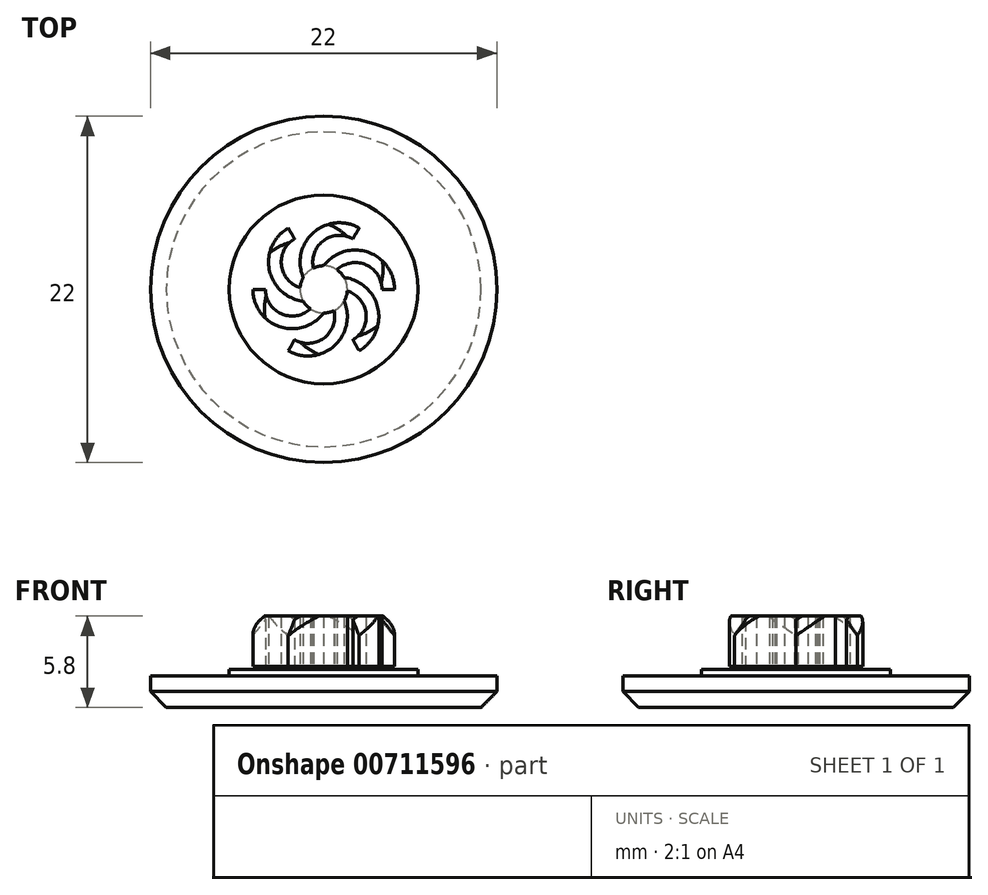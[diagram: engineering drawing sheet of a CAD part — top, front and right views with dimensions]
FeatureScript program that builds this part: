
annotation { "Feature Type Name" : "Feature", "Feature Type Description" : "" }
export const myFeature = defineFeature(function(context is Context, id is Id, definition is map)
    precondition{}
    {
        {
            var Q0;
            Q0=qCreatedBy(makeId("Top.planeOp"),FACE);
            var sketch = newSketch(context, id + "F0", { "sketchPlane" : qUnion([Q0])});
            skCircle(sketch, "E0", {"center": v(0, 0) * mm, "radius": 11 * mm});
            skSolve(sketch);
        }
        {
            var Q0;
            Q0=makeQuery(id+"F0.imprint","IMPRINT",FACE,{"disambiguationData":[TD([[makeQuery(id+"F0.imprint","IMPRINT",EDGE,{"derivedFrom":sQuery(id+"F0.wireOp",EDGE,"E0")}),1.0]])]});
            extrude(context, id + "F1", {"entities" : qUnion([Q0]), "depth" : 2 * mm, "offsetDistance" : 25 * mm});
        }
        {
            var Q0;
            Q0=makeQuery(id+"F1.opExtrude","CAP_EDGE",EDGE,{"disambiguationData":[OSD([sQuery(id+"F0.wireOp",EDGE,"E0")])],"isStart":true});
            chamfer(context, id + "F2", {"entities" : qUnion([Q0]), "width" : 1 * mm, "tangentPropagation" : true});
        }
        {
            var Q0;
            Q0=makeQuery(id+"F1.opExtrude","CAP_FACE",FACE,{"disambiguationData":[OSD([sQuery(id+"F0.wireOp",EDGE,"E0")])],"isStart":false});
            var sketch = newSketch(context, id + "F3", { "sketchPlane" : qUnion([Q0])});
            skCircle(sketch, "E1", {"center": v(0, 0) * mm, "radius": 6 * mm});
            skSolve(sketch);
        }
        {
            var Q0;
            Q0=makeQuery(id+"F3.imprint","IMPRINT",FACE,{"disambiguationData":[TD([[makeQuery(id+"F3.imprint","IMPRINT",EDGE,{"derivedFrom":sQuery(id+"F3.wireOp",EDGE,"E1")}),1.0]])]});
            extrude(context, id + "F4", {"entities" : qUnion([Q0]), "operationType" : NewBodyOperationType.ADD, "depth" : .4 * mm, "offsetDistance" : 25 * mm});
        }
        {
            var Q0;
            Q0=makeQuery(id+"F4.opExtrude","CAP_FACE",FACE,{"disambiguationData":[OSD([sQuery(id+"F3.wireOp",EDGE,"E1")])],"isStart":false});
            var sketch = newSketch(context, id + "F5", { "sketchPlane" : qUnion([Q0])});
            skCircle(sketch, "E2", {"center": v(0, 0) * mm, "radius": 4.5 * mm});
            skCircle(sketch, "E3", {"center": v(0, 0) * mm, "radius": 1.5 * mm});
            skCircle(sketch, "E4.0", {"center": v(0, 0) * mm, "radius": 11 * mm});
            skArc(sketch, "E5", {"start": v(4.5, 0) * mm, "mid": v(2.8, 2.37) * mm, "end": v(0, 1.5) * mm});
            skArc(sketch, "E6.0", {"start": v(3.7, 0) * mm, "mid": v(2.68, 1.56) * mm, "end": v(0.84, 1.24) * mm});
            skLineSegment(sketch, "E7", {"start": v(3.7, 0) * mm, "end": v(4.5, 0) * mm});
            skArc(sketch, "E8.1.0", {"start": v(1.85, 3.2) * mm, "mid": v(-0.01, 3.1) * mm, "end": v(-0.66, 1.35) * mm});
            skArc(sketch, "E8.1.1", {"start": v(2.25, 3.9) * mm, "mid": v(-0.66, 3.6) * mm, "end": v(-1.3, 0.75) * mm});
            skLineSegment(sketch, "E8.1.2", {"start": v(1.85, 3.2) * mm, "end": v(2.25, 3.9) * mm});
            skArc(sketch, "E8.2.0", {"start": v(-1.85, 3.2) * mm, "mid": v(-2.69, 1.54) * mm, "end": v(-1.5, 0.1) * mm});
            skArc(sketch, "E8.2.1", {"start": v(-2.25, 3.9) * mm, "mid": v(-3.45, 1.23) * mm, "end": v(-1.3, -0.75) * mm});
            skLineSegment(sketch, "E8.2.2", {"start": v(-1.85, 3.2) * mm, "end": v(-2.25, 3.9) * mm});
            skArc(sketch, "E8.3.0", {"start": v(-3.7, 0) * mm, "mid": v(-2.68, -1.56) * mm, "end": v(-0.84, -1.24) * mm});
            skArc(sketch, "E8.3.1", {"start": v(-4.5, 0) * mm, "mid": v(-2.8, -2.37) * mm, "end": v(0, -1.5) * mm});
            skLineSegment(sketch, "E8.3.2", {"start": v(-3.7, 0) * mm, "end": v(-4.5, 0) * mm});
            skArc(sketch, "E8.4.0", {"start": v(-1.85, -3.2) * mm, "mid": v(0.01, -3.1) * mm, "end": v(0.66, -1.35) * mm});
            skArc(sketch, "E8.4.1", {"start": v(-2.25, -3.9) * mm, "mid": v(0.66, -3.6) * mm, "end": v(1.3, -0.75) * mm});
            skLineSegment(sketch, "E8.4.2", {"start": v(-1.85, -3.2) * mm, "end": v(-2.25, -3.9) * mm});
            skArc(sketch, "E8.5.0", {"start": v(1.85, -3.2) * mm, "mid": v(2.69, -1.54) * mm, "end": v(1.5, -0.1) * mm});
            skArc(sketch, "E8.5.1", {"start": v(2.25, -3.9) * mm, "mid": v(3.45, -1.23) * mm, "end": v(1.3, 0.75) * mm});
            skLineSegment(sketch, "E8.5.2", {"start": v(1.85, -3.2) * mm, "end": v(2.25, -3.9) * mm});
            skSolve(sketch);
        }
        {
            var Q0;
            {var subQ0=sQuery(id+"F5.wireOp",EDGE,"E8.4.0");Q0=makeQuery(id+"F5.imprint","IMPRINT",FACE,{"disambiguationData":[TD([[makeQuery(id+"F5.imprint","IMPRINT",EDGE,{"derivedFrom":subQ0}),-1.0]])]});}
            var Q1;
            {var subQ0=sQuery(id+"F5.wireOp",EDGE,"E8.3.0");Q1=makeQuery(id+"F5.imprint","IMPRINT",FACE,{"disambiguationData":[TD([[makeQuery(id+"F5.imprint","IMPRINT",EDGE,{"derivedFrom":subQ0}),-1.0]])]});}
            var Q2;
            {var subQ0=sQuery(id+"F5.wireOp",EDGE,"E8.2.0");Q2=makeQuery(id+"F5.imprint","IMPRINT",FACE,{"disambiguationData":[TD([[makeQuery(id+"F5.imprint","IMPRINT",EDGE,{"derivedFrom":subQ0}),-1.0]])]});}
            var Q3;
            {var subQ0=sQuery(id+"F5.wireOp",EDGE,"E8.1.0");Q3=makeQuery(id+"F5.imprint","IMPRINT",FACE,{"disambiguationData":[TD([[makeQuery(id+"F5.imprint","IMPRINT",EDGE,{"derivedFrom":subQ0}),-1.0]])]});}
            var Q4;
            {var subQ0=sQuery(id+"F5.wireOp",EDGE,"E5");Q4=makeQuery(id+"F5.imprint","IMPRINT",FACE,{"disambiguationData":[TD([[makeQuery(id+"F5.imprint","IMPRINT",EDGE,{"derivedFrom":subQ0}),1.0]])]});}
            var Q5;
            {var subQ0=sQuery(id+"F5.wireOp",EDGE,"E8.5.0");Q5=makeQuery(id+"F5.imprint","IMPRINT",FACE,{"disambiguationData":[TD([[makeQuery(id+"F5.imprint","IMPRINT",EDGE,{"derivedFrom":subQ0}),-1.0]])]});}
            var Q6;
            {var subQ0=sQuery(id+"F5.wireOp",EDGE,"E3");var subQ8=makeQuery(id+"F5.imprint","INTERSECT",VERTEX,{"derivedFrom":[subQ0,sQuery(id+"F5.wireOp",EDGE,"E6.0")]});Q6=makeQuery(id+"F5.imprint","IMPRINT",FACE,{"disambiguationData":[TD([[makeQuery(id+"F5.imprint","IMPRINT",EDGE,{"disambiguationData":[TD([[subQ8,1.0]])],"derivedFrom":subQ0}),1.0]])]});}
            extrude(context, id + "F6", {"entities" : qUnion([Q0, Q1, Q2, Q3, Q4, Q5, Q6]), "operationType" : NewBodyOperationType.ADD, "depth" : 3.4 * mm, "offsetDistance" : 25 * mm});
        }
        {
            var Q0;
            {var subQ0=sQuery(id+"F5.wireOp",EDGE,"E8.4.0");Q0=makeQuery(id+"F5.imprint","IMPRINT",FACE,{"disambiguationData":[TD([[makeQuery(id+"F5.imprint","IMPRINT",EDGE,{"derivedFrom":subQ0}),-1.0]])]});}
            var Q1;
            {var subQ0=sQuery(id+"F5.wireOp",EDGE,"E8.3.0");Q1=makeQuery(id+"F5.imprint","IMPRINT",FACE,{"disambiguationData":[TD([[makeQuery(id+"F5.imprint","IMPRINT",EDGE,{"derivedFrom":subQ0}),-1.0]])]});}
            var Q2;
            {var subQ0=sQuery(id+"F5.wireOp",EDGE,"E8.2.0");Q2=makeQuery(id+"F5.imprint","IMPRINT",FACE,{"disambiguationData":[TD([[makeQuery(id+"F5.imprint","IMPRINT",EDGE,{"derivedFrom":subQ0}),-1.0]])]});}
            var Q3;
            {var subQ0=sQuery(id+"F5.wireOp",EDGE,"E8.1.0");Q3=makeQuery(id+"F5.imprint","IMPRINT",FACE,{"disambiguationData":[TD([[makeQuery(id+"F5.imprint","IMPRINT",EDGE,{"derivedFrom":subQ0}),-1.0]])]});}
            var Q4;
            {var subQ0=sQuery(id+"F5.wireOp",EDGE,"E5");Q4=makeQuery(id+"F5.imprint","IMPRINT",FACE,{"disambiguationData":[TD([[makeQuery(id+"F5.imprint","IMPRINT",EDGE,{"derivedFrom":subQ0}),1.0]])]});}
            var Q5;
            {var subQ0=sQuery(id+"F5.wireOp",EDGE,"E8.5.0");Q5=makeQuery(id+"F5.imprint","IMPRINT",FACE,{"disambiguationData":[TD([[makeQuery(id+"F5.imprint","IMPRINT",EDGE,{"derivedFrom":subQ0}),-1.0]])]});}
            extrude(context, id + "F7", {"entities" : qUnion([Q0, Q1, Q2, Q3, Q4, Q5]), "operationType" : NewBodyOperationType.REMOVE, "depth" : .2 * mm, "offsetDistance" : 25 * mm});
        }
        {
            var Q0;
            Q0=makeQuery(id+"F6.opExtrude","CAP_EDGE",EDGE,{"disambiguationData":[OSD([sQuery(id+"F5.wireOp",EDGE,"E8.5.2")])],"isStart":false});
            var Q1;
            Q1=makeQuery(id+"F6.opExtrude","CAP_EDGE",EDGE,{"disambiguationData":[OSD([sQuery(id+"F5.wireOp",EDGE,"E7")])],"isStart":false});
            var Q2;
            Q2=makeQuery(id+"F6.opExtrude","CAP_EDGE",EDGE,{"disambiguationData":[OSD([sQuery(id+"F5.wireOp",EDGE,"E8.4.2")])],"isStart":false});
            var Q3;
            Q3=makeQuery(id+"F6.opExtrude","CAP_EDGE",EDGE,{"disambiguationData":[OSD([sQuery(id+"F5.wireOp",EDGE,"E8.3.2")])],"isStart":false});
            var Q4;
            Q4=makeQuery(id+"F6.opExtrude","CAP_EDGE",EDGE,{"disambiguationData":[OSD([sQuery(id+"F5.wireOp",EDGE,"E8.1.2")])],"isStart":false});
            var Q5;
            Q5=makeQuery(id+"F6.opExtrude","CAP_EDGE",EDGE,{"disambiguationData":[OSD([sQuery(id+"F5.wireOp",EDGE,"E8.2.2")])],"isStart":false});
            chamfer(context, id + "F8", {"entities" : qUnion([Q0, Q1, Q2, Q3, Q4, Q5]), "width" : .1 * mm, "tangentPropagation" : true});
        }
        {
            var Q0;
            Q0=makeQuery(id+"F8.opChamfer","BLEND_EDGE",EDGE,{"blendedFrom":[makeQuery(id+"F6.opExtrude","CAP_EDGE",EDGE,{"disambiguationData":[OSD([sQuery(id+"F5.wireOp",EDGE,"E8.5.2")])],"isStart":false}),makeQuery(id+"F6.opExtrude","SWEPT_FACE",FACE,{"disambiguationData":[OSD([sQuery(id+"F5.wireOp",EDGE,"E8.5.1")])]})],"blendedInto":[makeQuery(id+"F6.opExtrude","SWEPT_FACE",FACE,{"disambiguationData":[OSD([sQuery(id+"F5.wireOp",EDGE,"E8.5.1")])]})]});
            var Q1;
            Q1=makeQuery(id+"F8.opChamfer","BLEND_EDGE",EDGE,{"blendedFrom":[makeQuery(id+"F6.opExtrude","CAP_EDGE",EDGE,{"disambiguationData":[OSD([sQuery(id+"F5.wireOp",EDGE,"E8.4.2")])],"isStart":false}),makeQuery(id+"F6.opExtrude","SWEPT_FACE",FACE,{"disambiguationData":[OSD([sQuery(id+"F5.wireOp",EDGE,"E8.4.1")])]})],"blendedInto":[makeQuery(id+"F6.opExtrude","SWEPT_FACE",FACE,{"disambiguationData":[OSD([sQuery(id+"F5.wireOp",EDGE,"E8.4.1")])]})]});
            var Q2;
            Q2=makeQuery(id+"F8.opChamfer","BLEND_EDGE",EDGE,{"blendedFrom":[makeQuery(id+"F6.opExtrude","CAP_EDGE",EDGE,{"disambiguationData":[OSD([sQuery(id+"F5.wireOp",EDGE,"E7")])],"isStart":false}),makeQuery(id+"F6.opExtrude","SWEPT_FACE",FACE,{"disambiguationData":[OSD([sQuery(id+"F5.wireOp",EDGE,"E5")])]})],"blendedInto":[makeQuery(id+"F6.opExtrude","SWEPT_FACE",FACE,{"disambiguationData":[OSD([sQuery(id+"F5.wireOp",EDGE,"E5")])]})]});
            var Q3;
            Q3=makeQuery(id+"F8.opChamfer","BLEND_EDGE",EDGE,{"blendedFrom":[makeQuery(id+"F6.opExtrude","CAP_EDGE",EDGE,{"disambiguationData":[OSD([sQuery(id+"F5.wireOp",EDGE,"E8.1.2")])],"isStart":false}),makeQuery(id+"F6.opExtrude","SWEPT_FACE",FACE,{"disambiguationData":[OSD([sQuery(id+"F5.wireOp",EDGE,"E8.1.1")])]})],"blendedInto":[makeQuery(id+"F6.opExtrude","SWEPT_FACE",FACE,{"disambiguationData":[OSD([sQuery(id+"F5.wireOp",EDGE,"E8.1.1")])]})]});
            var Q4;
            Q4=makeQuery(id+"F8.opChamfer","BLEND_EDGE",EDGE,{"blendedFrom":[makeQuery(id+"F6.opExtrude","CAP_EDGE",EDGE,{"disambiguationData":[OSD([sQuery(id+"F5.wireOp",EDGE,"E8.2.2")])],"isStart":false}),makeQuery(id+"F6.opExtrude","SWEPT_FACE",FACE,{"disambiguationData":[OSD([sQuery(id+"F5.wireOp",EDGE,"E8.2.1")])]})],"blendedInto":[makeQuery(id+"F6.opExtrude","SWEPT_FACE",FACE,{"disambiguationData":[OSD([sQuery(id+"F5.wireOp",EDGE,"E8.2.1")])]})]});
            var Q5;
            Q5=makeQuery(id+"F8.opChamfer","BLEND_EDGE",EDGE,{"blendedFrom":[makeQuery(id+"F6.opExtrude","CAP_EDGE",EDGE,{"disambiguationData":[OSD([sQuery(id+"F5.wireOp",EDGE,"E8.3.2")])],"isStart":false}),makeQuery(id+"F6.opExtrude","SWEPT_FACE",FACE,{"disambiguationData":[OSD([sQuery(id+"F5.wireOp",EDGE,"E8.3.1")])]})],"blendedInto":[makeQuery(id+"F6.opExtrude","SWEPT_FACE",FACE,{"disambiguationData":[OSD([sQuery(id+"F5.wireOp",EDGE,"E8.3.1")])]})]});
            chamfer(context, id + "F9", {"entities" : qUnion([Q0, Q1, Q2, Q3, Q4, Q5]), "width" : .8 * mm, "tangentPropagation" : true});
        }
    });
